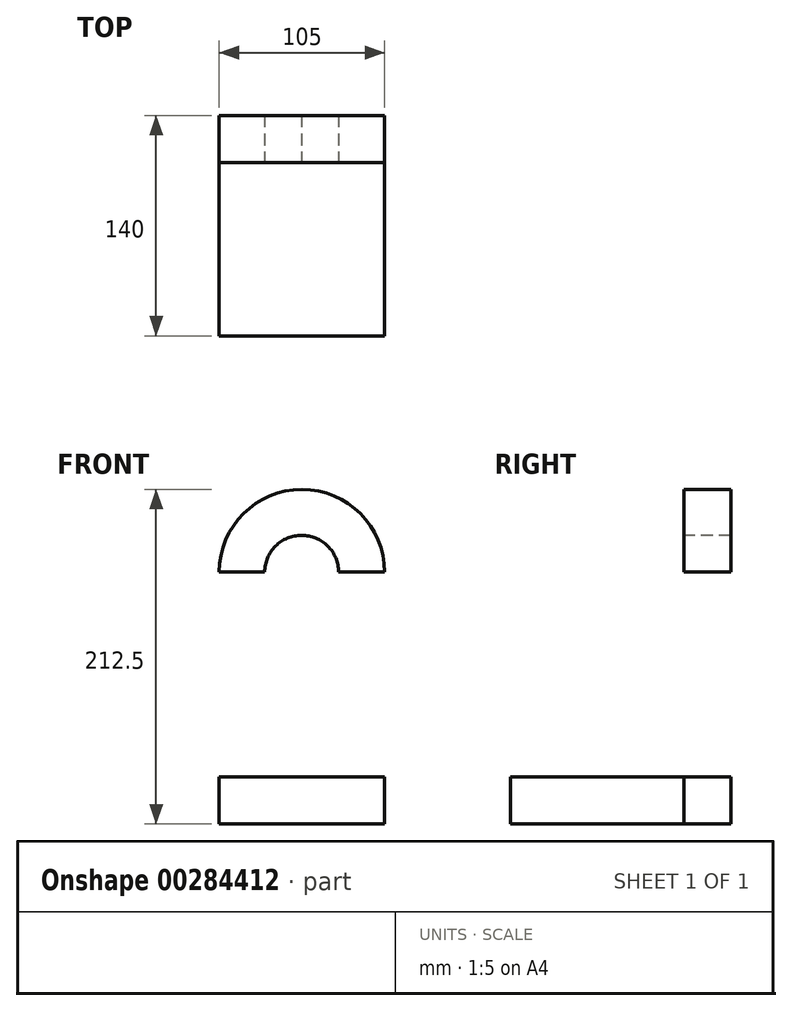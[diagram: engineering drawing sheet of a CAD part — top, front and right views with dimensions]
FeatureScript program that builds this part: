
annotation { "Feature Type Name" : "Feature", "Feature Type Description" : "" }
export const myFeature = defineFeature(function(context is Context, id is Id, definition is map)
    precondition{}
    {
        {
            var Q0;
            Q0=qCreatedBy(makeId("Front.planeOp"),FACE);
            var sketch = newSketch(context, id + "F0", { "sketchPlane" : qUnion([Q0])});
            skLineSegment(sketch, "E0.bottom", {"start": v(0, 0) * mm, "end": v(105, 0) * mm});
            skLineSegment(sketch, "E0.top", {"start": v(0, 160) * mm, "end": v(105, 160) * mm});
            skLineSegment(sketch, "E0.left", {"start": v(0, 0) * mm, "end": v(0, 160) * mm});
            skLineSegment(sketch, "E0.right", {"start": v(105, 0) * mm, "end": v(105, 160) * mm});
            skArc(sketch, "E1", {"start": v(105, 160) * mm, "mid": v(52.5, 212.5) * mm, "end": v(0, 160) * mm});
            skCircle(sketch, "E2", {"center": v(52.5, 160) * mm, "radius": 23.3 * mm});
            skLineSegment(sketch, "E3.top", {"start": v(0, 30) * mm, "end": v(105, 30) * mm});
            skLineSegment(sketch, "E3.left", {"start": v(0, 0) * mm, "end": v(0, 30) * mm});
            skLineSegment(sketch, "E3.right", {"start": v(105, 0) * mm, "end": v(105, 30) * mm});
            skSolve(sketch);
        }
        {
            var Q0;
            Q0=makeQuery(id+"F0.imprint","IMPRINT",FACE,{"disambiguationData":[TD([[makeQuery(id+"F0.imprint","IMPRINT",EDGE,{"derivedFrom":sQuery(id+"F0.wireOp",EDGE,"E0.bottom")}),1.0]])]});
            extrude(context, id + "F1", {"entities" : qUnion([Q0]), "depth" : 110 * mm, "hasSecondDirection" : true, "secondDirectionOppositeDirection" : true, "secondDirectionDepth" : 30 * mm});
        }
        {
            var Q0;
            {var subQ1=sQuery(id+"F0.wireOp",EDGE,"E0.left");Q0=makeQuery(id+"F0.imprint","IMPRINT",FACE,{"disambiguationData":[TD([[makeQuery(id+"F0.imprint","IMPRINT",EDGE,{"derivedFrom":subQ1}),-1.0]])]});}
            var Q1;
            {var subQ0=sQuery(id+"F0.wireOp",EDGE,"E1");Q1=makeQuery(id+"F0.imprint","IMPRINT",FACE,{"disambiguationData":[TD([[makeQuery(id+"F0.imprint","IMPRINT",EDGE,{"derivedFrom":subQ0}),1.0]])]});}
            extrude(context, id + "F2", {"entities" : qUnion([Q0, Q1]), "oppositeDirection" : true, "depth" : 30 * mm});
        }
        {
            var Q0;
            Q0=makeQuery(id+"Fbk37QOuQ3WjLU5_2.boolean.opBoolean","MERGE",FACE,{"derivedFrom":[makeQuery(id+"F1.opExtrude","CAP_FACE",FACE,{"disambiguationData":[OSD([sQuery(id+"F0.wireOp",EDGE,"E0.bottom"),sQuery(id+"F0.wireOp",EDGE,"E3.top"),sQuery(id+"F0.wireOp",EDGE,"E3.left"),sQuery(id+"F0.wireOp",EDGE,"E3.right")])],"isStart":false}),makeQuery(id+"Fbk37QOuQ3WjLU5_2.opExtrude","SWEPT_FACE",FACE,{"disambiguationData":[OSD([sQuery(id+"FRzlaZDm9ym3Mtf_2.wireOp",EDGE,"bG4zQvKH-2FVC-vom4-cUI7-WdxKsPs4mKzB.bottom")])]})]});
            var sketch = newSketch(context, id + "F3", { "sketchPlane" : qUnion([Q0])});
            skCircle(sketch, "E4", {"center": v(52.16, 160) * mm, "radius": 23.3 * mm});
            skSolve(sketch);
        }
        {
            var Q0;
            Q0 = qSketchRegion(id + "F3", true);
            extrude(context, id + "F4", {"entities" : qUnion([Q0]), "operationType" : NewBodyOperationType.REMOVE, "endBound" : BoundingType.THROUGH_ALL, "oppositeDirection" : true, "depth" : 25 * mm});
        }
    });
